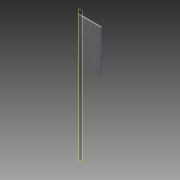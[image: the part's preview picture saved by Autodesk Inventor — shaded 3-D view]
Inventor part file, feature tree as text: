
AUTODESK INVENTOR PART (.ipt)
format: ipt  version: 2015 (Build 190159000, 159)  size: 104,448 bytes
history: native  units: in
note: dims shown in document units (in); Inventor stores cm internally (conversion verified against a paired STEP export)
features: reference x19, plane x1, extrude x1, sketch x1
ambient origin geometry x8: Origin, YZ Plane, XZ Plane, XY Plane, X Axis, Y Axis, Z Axis, Center Point
bodies: Solid1 (feature_tree)
feature tree (22):
  plane  "Work Plane1"
  extrude  "Extrusion1"  [1 undecoded]
  sketch  "Sketch1"  dims[d0=0.25in d1=0.0in]
  reference  "Reference1"
  reference  "Reference2"
  reference  "Reference3"
  reference  "Reference4"
  reference  "Reference5"
  reference  "Reference6"
  reference  "Reference7"
  reference  "Reference8"
  reference  "Reference9"
  reference  "Reference10"
  reference  "Reference11"
  reference  "Reference12"
  reference  "Reference13"
  reference  "Reference14"
  reference  "Reference15"
  reference  "Reference16"
  reference  "Reference17"
  reference  "Reference18"
  reference  "Reference19"
note: 1 required parameter value undecoded (feature->parameter linkage not recoverable at this tier; creation-order binding heuristic only, values carry confidence <= 0.55)
